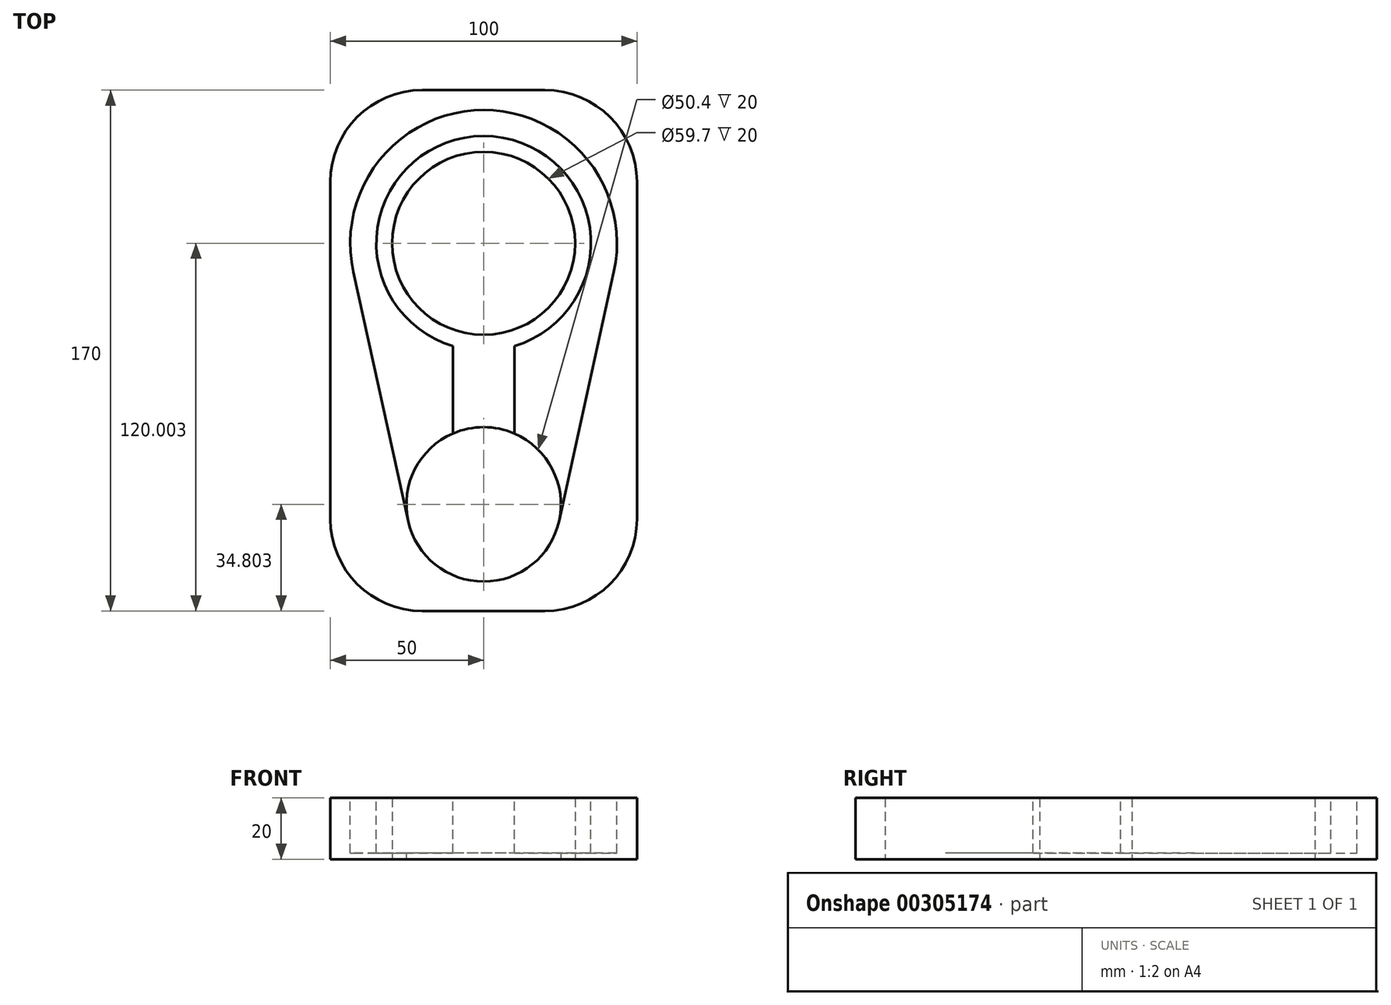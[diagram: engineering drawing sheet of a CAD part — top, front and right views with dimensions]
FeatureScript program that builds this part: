
annotation { "Feature Type Name" : "Feature", "Feature Type Description" : "" }
export const myFeature = defineFeature(function(context is Context, id is Id, definition is map)
    precondition{}
    {
        {
            var Q0;
            Q0=qCreatedBy(makeId("Top.planeOp"),FACE);
            var sketch = newSketch(context, id + "F0", { "sketchPlane" : qUnion([Q0])});
            skArc(sketch, "E0.0", {"start": v(50, 57.53) * mm, "mid": v(41.21, 78.75) * mm, "end": v(20, 87.53) * mm});
            skArc(sketch, "E0.1", {"start": v(-50, -52.47) * mm, "mid": v(-41.21, -73.68) * mm, "end": v(-20, -82.47) * mm});
            skArc(sketch, "E0.2", {"start": v(20, -82.47) * mm, "mid": v(41.21, -73.68) * mm, "end": v(50, -52.47) * mm});
            skArc(sketch, "E0.3", {"start": v(-20, 87.53) * mm, "mid": v(-41.21, 78.75) * mm, "end": v(-50, 57.53) * mm});
            skCircle(sketch, "E0.4", {"center": v(0, -47.67) * mm, "radius": 25.2 * mm});
            skCircle(sketch, "E0.5", {"center": v(0, 37.53) * mm, "radius": 29.85 * mm});
            skLineSegment(sketch, "E1", {"start": v(-50, 57.53) * mm, "end": v(-50, -52.47) * mm});
            skLineSegment(sketch, "E2", {"start": v(-20, -82.47) * mm, "end": v(20, -82.47) * mm});
            skLineSegment(sketch, "E3", {"start": v(-20, 87.53) * mm, "end": v(20, 87.53) * mm});
            skLineSegment(sketch, "E4", {"start": v(50, -52.47) * mm, "end": v(50, 57.53) * mm});
            skSolve(sketch);
        }
        {
            var Q0;
            Q0=makeQuery(id+"F0.imprint","IMPRINT",FACE,{"disambiguationData":[TD([[makeQuery(id+"F0.imprint","IMPRINT",EDGE,{"derivedFrom":sQuery(id+"F0.wireOp",EDGE,"E0.0")}),1.0]])]});
            extrude(context, id + "F1", {"entities" : qUnion([Q0]), "depth" : 20 * mm, "offsetDistance" : 25 * mm});
        }
        {
            var Q0;
            Q0=makeQuery(id+"F1.opExtrude","CAP_FACE",FACE,{"disambiguationData":[OSD([sQuery(id+"F0.wireOp",EDGE,"E0.0"),sQuery(id+"F0.wireOp",EDGE,"E0.1"),sQuery(id+"F0.wireOp",EDGE,"E0.2"),sQuery(id+"F0.wireOp",EDGE,"E0.3"),sQuery(id+"F0.wireOp",EDGE,"E0.4"),sQuery(id+"F0.wireOp",EDGE,"E0.5"),sQuery(id+"F0.wireOp",EDGE,"E1"),sQuery(id+"F0.wireOp",EDGE,"E2"),sQuery(id+"F0.wireOp",EDGE,"E3"),sQuery(id+"F0.wireOp",EDGE,"E4")])],"isStart":false});
            var sketch = newSketch(context, id + "F2", { "sketchPlane" : qUnion([Q0])});
            skArc(sketch, "E5", {"start": v(42.48, 28.2) * mm, "mid": v(0, 81.03) * mm, "end": v(-42.48, 28.2) * mm});
            skLineSegment(sketch, "E6", {"start": v(-42.48, 28.2) * mm, "end": v(-24.61, -53.08) * mm});
            skLineSegment(sketch, "E7", {"start": v(24.61, -53.08) * mm, "end": v(42.48, 28.2) * mm});
            skArc(sketch, "E8.0", {"start": v(-24.61, -53.08) * mm, "mid": v(0, -72.87) * mm, "end": v(24.61, -53.08) * mm});
            skLineSegment(sketch, "E9.0", {"start": v(-10, -24.54) * mm, "end": v(-10, 4) * mm});
            skLineSegment(sketch, "E10.0", {"start": v(10, -24.54) * mm, "end": v(10, 4) * mm});
            skArc(sketch, "E11.trimOffspring", {"start": v(10, -24.54) * mm, "mid": v(0, -22.47) * mm, "end": v(-10, -24.54) * mm});
            skCircle(sketch, "E12", {"center": v(0, 37.53) * mm, "radius": 35 * mm});
            skSolve(sketch);
        }
        {
            var Q0;
            Q0=makeQuery(id+"F2.imprint","IMPRINT",FACE,{"disambiguationData":[TD([[makeQuery(id+"F2.imprint","IMPRINT",EDGE,{"derivedFrom":sQuery(id+"F2.wireOp",EDGE,"E5")}),1.0]])]});
            extrude(context, id + "F3", {"entities" : qUnion([Q0]), "operationType" : NewBodyOperationType.REMOVE, "oppositeDirection" : true, "depth" : 18 * mm, "offsetDistance" : 25 * mm});
        }
    });
